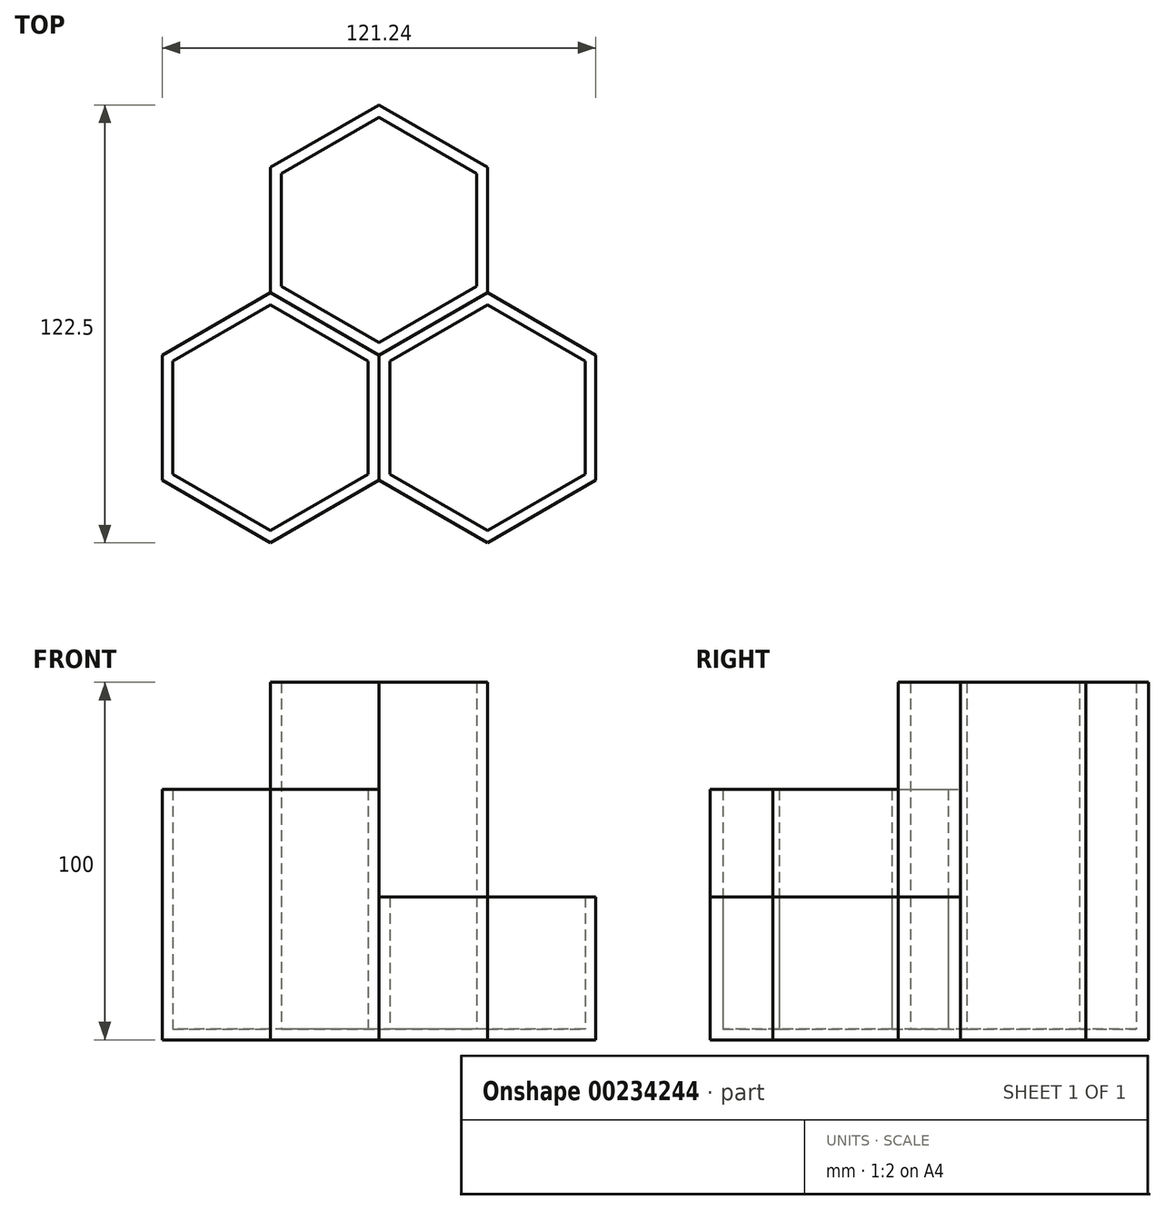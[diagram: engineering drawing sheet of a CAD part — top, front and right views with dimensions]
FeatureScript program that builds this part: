
annotation { "Feature Type Name" : "Feature", "Feature Type Description" : "" }
export const myFeature = defineFeature(function(context is Context, id is Id, definition is map)
    precondition{}
    {
        {
            var Q0;
            Q0=qCreatedBy(makeId("Top.planeOp"),FACE);
            var sketch = newSketch(context, id + "F0", { "sketchPlane" : qUnion([Q0])});
            skCircle(sketch, "E0.cCircle", {"center": v(0, 0) * mm, "radius": 30.31 * mm, "construction": true});
            skLineSegment(sketch, "E0.0", {"start": v(30.31, -17.5) * mm, "end": v(0, -35) * mm});
            skLineSegment(sketch, "E0.1", {"start": v(0, -35) * mm, "end": v(-30.31, -17.5) * mm});
            skLineSegment(sketch, "E0.2", {"start": v(-30.31, -17.5) * mm, "end": v(-30.31, 17.5) * mm});
            skLineSegment(sketch, "E0.3", {"start": v(-30.31, 17.5) * mm, "end": v(0, 35) * mm});
            skLineSegment(sketch, "E0.4", {"start": v(0, 35) * mm, "end": v(30.31, 17.5) * mm});
            skLineSegment(sketch, "E0.5", {"start": v(30.31, 17.5) * mm, "end": v(30.31, -17.5) * mm});
            skPoint(sketch, "E0.0.midPoint", {"position": v(15.16, -26.25) * mm});
            skCircle(sketch, "E1.cCircle", {"center": v(-30.31, -52.5) * mm, "radius": 30.31 * mm, "construction": true});
            skLineSegment(sketch, "E1.0", {"start": v(0, -70) * mm, "end": v(-30.31, -87.5) * mm});
            skLineSegment(sketch, "E1.1", {"start": v(-30.31, -87.5) * mm, "end": v(-60.62, -70) * mm});
            skLineSegment(sketch, "E1.2", {"start": v(-60.62, -70) * mm, "end": v(-60.62, -35) * mm});
            skLineSegment(sketch, "E1.3", {"start": v(-60.62, -35) * mm, "end": v(-30.31, -17.5) * mm});
            skLineSegment(sketch, "E1.4", {"start": v(-30.31, -17.5) * mm, "end": v(0, -35) * mm});
            skLineSegment(sketch, "E1.5", {"start": v(0, -35) * mm, "end": v(0, -70) * mm});
            skPoint(sketch, "E1.0.midPoint", {"position": v(-15.15, -78.75) * mm});
            skCircle(sketch, "E2.cCircle", {"center": v(30.31, -52.5) * mm, "radius": 30.31 * mm, "construction": true});
            skLineSegment(sketch, "E2.0", {"start": v(30.31, -87.5) * mm, "end": v(0, -70) * mm});
            skLineSegment(sketch, "E2.1", {"start": v(0, -70) * mm, "end": v(0, -35) * mm});
            skLineSegment(sketch, "E2.2", {"start": v(0, -35) * mm, "end": v(30.31, -17.5) * mm});
            skLineSegment(sketch, "E2.3", {"start": v(30.31, -17.5) * mm, "end": v(60.62, -35) * mm});
            skLineSegment(sketch, "E2.4", {"start": v(60.62, -35) * mm, "end": v(60.62, -70) * mm});
            skLineSegment(sketch, "E2.5", {"start": v(60.62, -70) * mm, "end": v(30.31, -87.5) * mm});
            skPoint(sketch, "E2.0.midPoint", {"position": v(15.16, -78.75) * mm});
            skSolve(sketch);
        }
        {
            var Q0;
            Q0=makeQuery(id+"F0.imprint","IMPRINT",FACE,{"disambiguationData":[TD([[makeQuery(id+"F0.imprint","IMPRINT",EDGE,{"derivedFrom":sQuery(id+"F0.wireOp",EDGE,"E0.2")}),-1.0]])]});
            extrude(context, id + "F1", {"entities" : qUnion([Q0]), "depth" : 100 * mm});
        }
        {
            var Q0;
            Q0=makeQuery(id+"F0.imprint","IMPRINT",FACE,{"disambiguationData":[TD([[makeQuery(id+"F0.imprint","IMPRINT",EDGE,{"derivedFrom":sQuery(id+"F0.wireOp",EDGE,"E1.0")}),-1.0]])]});
            extrude(context, id + "F2", {"entities" : qUnion([Q0]), "depth" : 70 * mm});
        }
        {
            var Q0;
            Q0=makeQuery(id+"F0.imprint","IMPRINT",FACE,{"disambiguationData":[TD([[makeQuery(id+"F0.imprint","IMPRINT",EDGE,{"derivedFrom":sQuery(id+"F0.wireOp",EDGE,"E2.0")}),-1.0]])]});
            extrude(context, id + "F3", {"entities" : qUnion([Q0]), "depth" : 40 * mm});
        }
        {
            var Q0;
            Q0=makeQuery(id+"F2.opExtrude","CAP_FACE",FACE,{"disambiguationData":[OSD([sQuery(id+"F0.wireOp",EDGE,"E1.0"),sQuery(id+"F0.wireOp",EDGE,"E1.1"),sQuery(id+"F0.wireOp",EDGE,"E1.2"),sQuery(id+"F0.wireOp",EDGE,"E1.3"),sQuery(id+"F0.wireOp",EDGE,"E1.4"),sQuery(id+"F0.wireOp",EDGE,"E2.1")])],"isStart":false});
            var Q1;
            Q1=makeQuery(id+"F1.opExtrude","CAP_FACE",FACE,{"disambiguationData":[OSD([sQuery(id+"F0.wireOp",EDGE,"E0.2"),sQuery(id+"F0.wireOp",EDGE,"E0.3"),sQuery(id+"F0.wireOp",EDGE,"E0.4"),sQuery(id+"F0.wireOp",EDGE,"E0.5"),sQuery(id+"F0.wireOp",EDGE,"E1.4"),sQuery(id+"F0.wireOp",EDGE,"E2.2")])],"isStart":false});
            var Q2;
            Q2=makeQuery(id+"F3.opExtrude","CAP_FACE",FACE,{"disambiguationData":[OSD([sQuery(id+"F0.wireOp",EDGE,"E2.0"),sQuery(id+"F0.wireOp",EDGE,"E2.1"),sQuery(id+"F0.wireOp",EDGE,"E2.2"),sQuery(id+"F0.wireOp",EDGE,"E2.3"),sQuery(id+"F0.wireOp",EDGE,"E2.4"),sQuery(id+"F0.wireOp",EDGE,"E2.5")])],"isStart":false});
            shell(context, id + "F4", {"entities" : qUnion([Q0, Q1, Q2]), "thickness" : 3 * mm});
        }
    });
